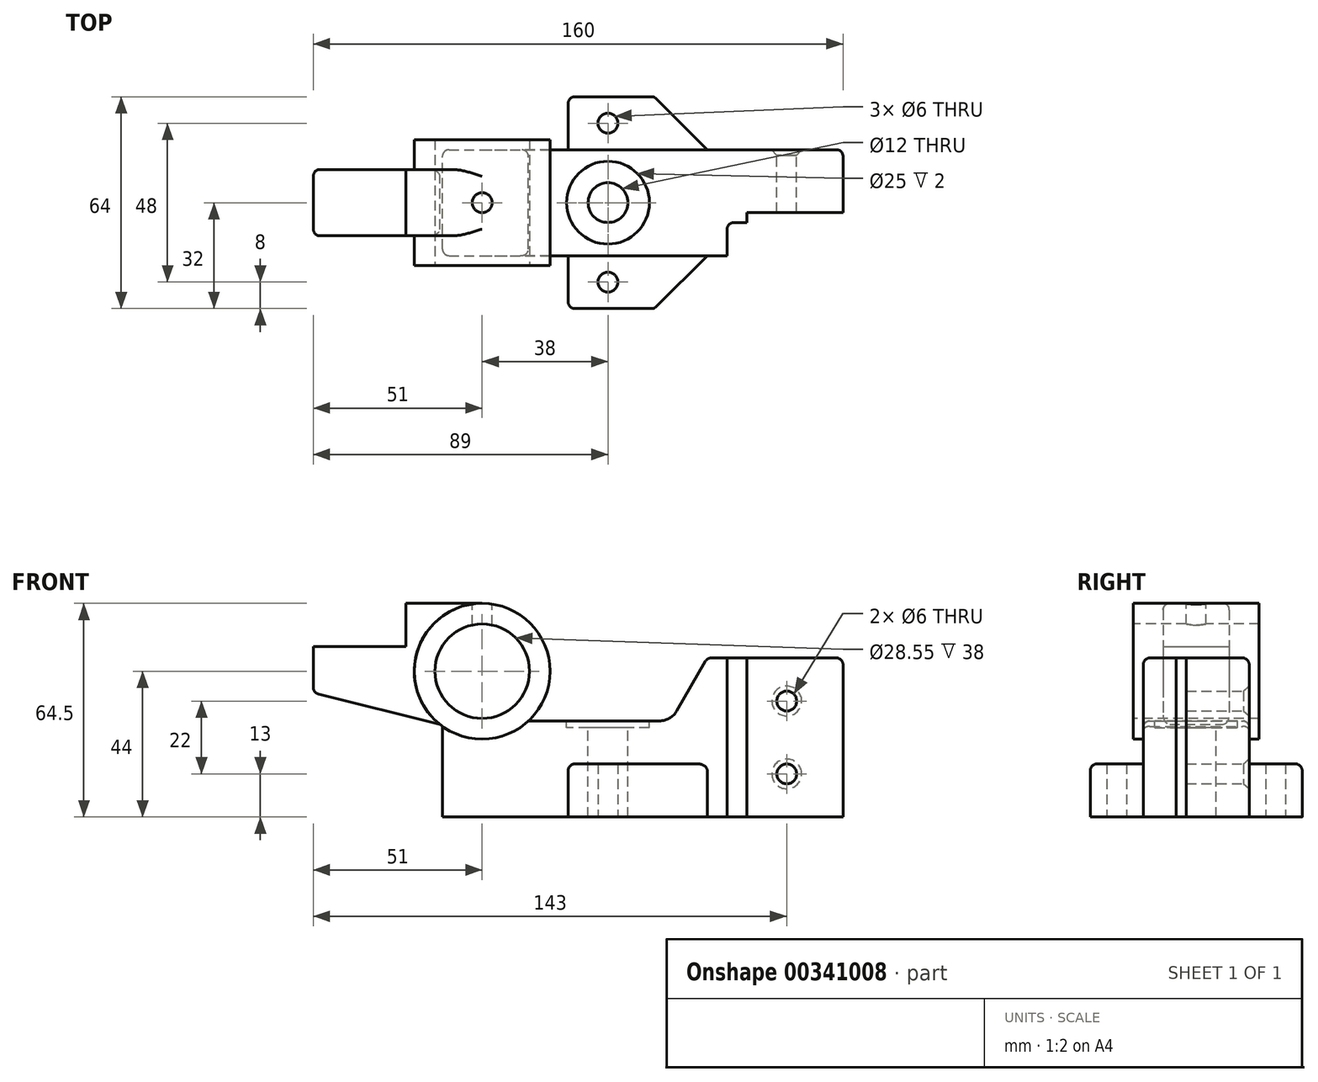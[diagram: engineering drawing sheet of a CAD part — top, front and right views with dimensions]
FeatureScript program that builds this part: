
annotation { "Feature Type Name" : "Feature", "Feature Type Description" : "" }
export const myFeature = defineFeature(function(context is Context, id is Id, definition is map)
    precondition{}
    {
        {
            var Q0;
            Q0=qCreatedBy(makeId("Front.planeOp"),FACE);
            var sketch = newSketch(context, id + "F0", { "sketchPlane" : qUnion([Q0])});
            skLineSegment(sketch, "E0", {"start": v(0, 0) * mm, "end": v(0, 48) * mm});
            skLineSegment(sketch, "E1", {"start": v(0, 48) * mm, "end": v(-41, 48) * mm});
            skLineSegment(sketch, "E2", {"start": v(-41, 48) * mm, "end": v(-50.24, 32) * mm});
            skLineSegment(sketch, "E3", {"start": v(-55.43, 29) * mm, "end": v(-95.03, 29) * mm});
            skLineSegment(sketch, "E4", {"start": v(-109, 64.5) * mm, "end": v(-132, 64.5) * mm});
            skLineSegment(sketch, "E5", {"start": v(-132, 64.5) * mm, "end": v(-132, 51.5) * mm});
            skLineSegment(sketch, "E6", {"start": v(-132, 51.5) * mm, "end": v(-160, 51.5) * mm});
            skLineSegment(sketch, "E7", {"start": v(-160, 51.5) * mm, "end": v(-160, 37.5) * mm});
            skLineSegment(sketch, "E8", {"start": v(-160, 37.5) * mm, "end": v(-121.78, 27.97) * mm});
            skLineSegment(sketch, "E9", {"start": v(-121, 27.38) * mm, "end": v(-121, 0) * mm});
            skLineSegment(sketch, "E10", {"start": v(-121, 0) * mm, "end": v(0, 0) * mm});
            skCircle(sketch, "E11", {"center": v(-109, 44) * mm, "radius": 20.5 * mm});
            skPoint(sketch, "E12.visualSharp", {"position": v(-51.97, 29) * mm});
            skArc(sketch, "E13.filletArc", {"start": v(-55.43, 29) * mm, "mid": v(-52.43, 29.8) * mm, "end": v(-50.24, 32) * mm});
            skSolve(sketch);
        }
        {
            var Q0;
            Q0=makeQuery(id+"F0.imprint","IMPRINT",FACE,{"disambiguationData":[TD([[makeQuery(id+"F0.imprint","IMPRINT",EDGE,{"derivedFrom":sQuery(id+"F0.wireOp",EDGE,"E0")}),1.0]])]});
            var Q1;
            {var subQ0=sQuery(id+"F0.wireOp",EDGE,"E11");var subQ1=makeQuery(id+"F0.imprint","INTERSECT",VERTEX,{"derivedFrom":[sQuery(id+"F0.wireOp",EDGE,"E4"),subQ0]});Q1=makeQuery(id+"F0.imprint","IMPRINT",FACE,{"disambiguationData":[TD([[makeQuery(id+"F0.imprint","IMPRINT",EDGE,{"disambiguationData":[TD([[subQ1,-1.0]])],"derivedFrom":subQ0}),1.0]])]});}
            extrude(context, id + "F1", {"entities" : qUnion([Q0, Q1]), "depth" : 32 * mm});
        }
        {
            var Q0;
            {var subQ0=sQuery(id+"F0.wireOp",EDGE,"E11");var subQ1=makeQuery(id+"F0.imprint","INTERSECT",VERTEX,{"derivedFrom":[sQuery(id+"F0.wireOp",EDGE,"E4"),subQ0]});Q0=makeQuery(id+"F0.imprint","IMPRINT",FACE,{"disambiguationData":[TD([[makeQuery(id+"F0.imprint","IMPRINT",EDGE,{"disambiguationData":[TD([[subQ1,-1.0]])],"derivedFrom":subQ0}),1.0]])]});}
            extrude(context, id + "F2", {"entities" : qUnion([Q0]), "operationType" : NewBodyOperationType.ADD, "depth" : 35 * mm, "hasSecondDirection" : true, "secondDirectionOppositeDirection" : true, "secondDirectionDepth" : 3 * mm});
        }
        {
            var Q0;
            {var subQ0=sQuery(id+"F0.wireOp",EDGE,"E4");Q0=makeQuery(id+"F0.imprint","IMPRINT",FACE,{"disambiguationData":[TD([[makeQuery(id+"F0.imprint","IMPRINT",EDGE,{"derivedFrom":subQ0}),1.0]])]});}
            extrude(context, id + "F3", {"entities" : qUnion([Q0]), "operationType" : NewBodyOperationType.ADD, "depth" : 26 * mm, "hasSecondDirection" : true, "secondDirectionOppositeDirection" : false, "secondDirectionDepth" : 6 * mm});
        }
        {
            var Q0;
            Q0=makeQuery(id+"F1.opExtrude","SWEPT_FACE",FACE,{"disambiguationData":[OSD([sQuery(id+"F0.wireOp",EDGE,"E1")])]});
            var sketch = newSketch(context, id + "F4", { "sketchPlane" : qUnion([Q0])});
            skLineSegment(sketch, "E14", {"start": v(0, -19) * mm, "end": v(-29, -19) * mm});
            skLineSegment(sketch, "E15", {"start": v(-29, -19) * mm, "end": v(-29, -22) * mm});
            skLineSegment(sketch, "E16", {"start": v(-29, -22) * mm, "end": v(-35, -22) * mm});
            skLineSegment(sketch, "E17", {"start": v(-35, -22) * mm, "end": v(-35, -32) * mm});
            skSolve(sketch);
        }
        {
            var Q0;
            {var subQ1=sQuery(id+"F4.wireOp",EDGE,"E14");Q0=makeQuery(id+"F4.imprint","IMPRINT",FACE,{"disambiguationData":[TD([[makeQuery(id+"F4.imprint","IMPRINT",EDGE,{"derivedFrom":subQ1}),1.0]])]});}
            extrude(context, id + "F5", {"entities" : qUnion([Q0]), "operationType" : NewBodyOperationType.REMOVE, "endBound" : BoundingType.THROUGH_ALL, "oppositeDirection" : true, "depth" : 25 * mm});
        }
        {
            var Q0;
            Q0=makeQuery(id+"F2.opExtrude","CAP_FACE",FACE,{"disambiguationData":[OSD([sQuery(id+"F0.wireOp",EDGE,"E11")])],"isStart":false});
            var sketch = newSketch(context, id + "F6", { "sketchPlane" : qUnion([Q0])});
            skCircle(sketch, "E18.0", {"center": v(-109, 44) * mm, "radius": 20.5 * mm});
            skSolve(sketch);
        }
        {
            var Q0;
            Q0=sQuery(id+"F6.wireOp",VERTEX,"E18.0.center");
            var Q1;
            Q1=makeQuery(id+"F1.opExtrude","SWEPT_BODY",BODY,{"disambiguationData":[OSD([sQuery(id+"F0.wireOp",EDGE,"E0"),sQuery(id+"F0.wireOp",EDGE,"E1"),sQuery(id+"F0.wireOp",EDGE,"E2"),sQuery(id+"F0.wireOp",EDGE,"E3"),sQuery(id+"F0.wireOp",EDGE,"E4"),sQuery(id+"F0.wireOp",EDGE,"E5"),sQuery(id+"F0.wireOp",EDGE,"E6"),sQuery(id+"F0.wireOp",EDGE,"E7"),sQuery(id+"F0.wireOp",EDGE,"E8"),sQuery(id+"F0.wireOp",EDGE,"E9"),sQuery(id+"F0.wireOp",EDGE,"E10"),sQuery(id+"F0.wireOp",EDGE,"E11"),sQuery(id+"F0.wireOp",EDGE,"E12.filletArc")])]});
            hole(context, id + "F7", {"style" : HoleStyle.SIMPLE, "endStyle" : HoleEndStyle.THROUGH, "holeDiameter" : 28.55 * mm, "tappedDepth" : 12 * mm, "tapClearance" : 3, "locations" : qUnion([Q0]), "scope" : qUnion([Q1])});
        }
        {
            var Q0;
            Q0=makeQuery(id+"F3.opExtrude","SWEPT_FACE",FACE,{"disambiguationData":[OSD([sQuery(id+"F0.wireOp",EDGE,"E4")])]});
            var sketch = newSketch(context, id + "F8", { "sketchPlane" : qUnion([Q0])});
            skPoint(sketch, "E19.endSnap0", {"position": v(-109, -16) * mm});
            skSolve(sketch);
        }
        {
            var Q0;
            Q0=sQuery(id+"F8.wireOp",VERTEX,"E19.endSnap0");
            var Q1;
            Q1=makeQuery(id+"F1.opExtrude","SWEPT_BODY",BODY,{"disambiguationData":[OSD([sQuery(id+"F0.wireOp",EDGE,"E0"),sQuery(id+"F0.wireOp",EDGE,"E1"),sQuery(id+"F0.wireOp",EDGE,"E2"),sQuery(id+"F0.wireOp",EDGE,"E3"),sQuery(id+"F0.wireOp",EDGE,"E4"),sQuery(id+"F0.wireOp",EDGE,"E5"),sQuery(id+"F0.wireOp",EDGE,"E6"),sQuery(id+"F0.wireOp",EDGE,"E7"),sQuery(id+"F0.wireOp",EDGE,"E8"),sQuery(id+"F0.wireOp",EDGE,"E9"),sQuery(id+"F0.wireOp",EDGE,"E10"),sQuery(id+"F0.wireOp",EDGE,"E11"),sQuery(id+"F0.wireOp",EDGE,"E12.filletArc")])]});
            hole(context, id + "F9", {"style" : HoleStyle.SIMPLE, "endStyle" : HoleEndStyle.BLIND, "holeDiameter" : 6 * mm, "holeDepth" : 12 * mm, "tappedDepth" : 12 * mm, "tapClearance" : 3, "locations" : qUnion([Q0]), "scope" : qUnion([Q1])});
        }
        {
            var Q0;
            Q0=makeQuery(id+"F1.opExtrude","SWEPT_FACE",FACE,{"disambiguationData":[OSD([sQuery(id+"F0.wireOp",EDGE,"E3")])]});
            var sketch = newSketch(context, id + "F10", { "sketchPlane" : qUnion([Q0])});
            skPoint(sketch, "E20.end.orphan", {"position": v(-71, -16) * mm});
            skPoint(sketch, "E20.start.orphan", {"position": v(-55.43, -16) * mm});
            skCircle(sketch, "E21.0", {"center": v(-109, -16) * mm, "radius": 3 * mm});
            skSolve(sketch);
        }
        {
            var Q0;
            Q0=sQuery(id+"F10.wireOp",VERTEX,"E20.end.orphan");
            var Q1;
            Q1=makeQuery(id+"F1.opExtrude","SWEPT_BODY",BODY,{"disambiguationData":[OSD([sQuery(id+"F0.wireOp",EDGE,"E0"),sQuery(id+"F0.wireOp",EDGE,"E1"),sQuery(id+"F0.wireOp",EDGE,"E2"),sQuery(id+"F0.wireOp",EDGE,"E3"),sQuery(id+"F0.wireOp",EDGE,"E4"),sQuery(id+"F0.wireOp",EDGE,"E5"),sQuery(id+"F0.wireOp",EDGE,"E6"),sQuery(id+"F0.wireOp",EDGE,"E7"),sQuery(id+"F0.wireOp",EDGE,"E8"),sQuery(id+"F0.wireOp",EDGE,"E9"),sQuery(id+"F0.wireOp",EDGE,"E10"),sQuery(id+"F0.wireOp",EDGE,"E11"),sQuery(id+"F0.wireOp",EDGE,"E12.filletArc")])]});
            hole(context, id + "F11", {"style" : HoleStyle.C_BORE, "endStyle" : HoleEndStyle.THROUGH, "holeDiameter" : 12 * mm, "cBoreDiameter" : 25 * mm, "cBoreDepth" : 2 * mm, "tappedDepth" : 12 * mm, "tapClearance" : 3, "locations" : qUnion([Q0]), "scope" : qUnion([Q1])});
        }
        {
            var Q0;
            {var subQ0=sQuery(id+"F0.wireOp",EDGE,"E2");var subQ1=sQuery(id+"F0.wireOp",EDGE,"E12.filletArc");var subQ2=sQuery(id+"F0.wireOp",EDGE,"E11");var subQ3=sQuery(id+"F0.wireOp",EDGE,"E1");var subQ4=sQuery(id+"F0.wireOp",EDGE,"E3");var subQ5=sQuery(id+"F0.wireOp",EDGE,"E4");var subQ6=sQuery(id+"F0.wireOp",EDGE,"E0");var subQ7=sQuery(id+"F0.wireOp",EDGE,"E9");var subQ8=sQuery(id+"F0.wireOp",EDGE,"E10");var subQ9=sQuery(id+"F0.wireOp",EDGE,"E8");Q0=makeQuery(id+"F2.boolean.opBoolean","SPLIT",FACE,{"disambiguationData":[TD([makeQuery(id+"F1.opExtrude","SWEPT_FACE",FACE,{"disambiguationData":[OSD([subQ6])]})])],"derivedFrom":makeQuery(id+"F1.opExtrude","CAP_FACE",FACE,{"disambiguationData":[OSD([subQ6,subQ3,subQ0,subQ4,subQ5,sQuery(id+"F0.wireOp",EDGE,"E5"),sQuery(id+"F0.wireOp",EDGE,"E6"),sQuery(id+"F0.wireOp",EDGE,"E7"),subQ9,subQ7,subQ8,subQ2,subQ1])],"isStart":true})});}
            var sketch = newSketch(context, id + "F12", { "sketchPlane" : qUnion([Q0])});
            skPoint(sketch, "E22.0", {"position": v(71, 29) * mm});
            skLineSegment(sketch, "E23", {"start": v(17, 48) * mm, "end": v(17, 0) * mm, "construction": true});
            skLineSegment(sketch, "E24", {"start": v(0, 13) * mm, "end": v(17, 13) * mm, "construction": true});
            skLineSegment(sketch, "E25", {"start": v(0, 35) * mm, "end": v(17, 35) * mm, "construction": true});
            skSolve(sketch);
        }
        {
            var Q0;
            Q0=sQuery(id+"F12.wireOp",VERTEX,"E25.end");
            var Q1;
            Q1=sQuery(id+"F12.wireOp",VERTEX,"E24.end");
            var Q2;
            Q2=makeQuery(id+"F1.opExtrude","SWEPT_BODY",BODY,{"disambiguationData":[OSD([sQuery(id+"F0.wireOp",EDGE,"E0"),sQuery(id+"F0.wireOp",EDGE,"E1"),sQuery(id+"F0.wireOp",EDGE,"E2"),sQuery(id+"F0.wireOp",EDGE,"E3"),sQuery(id+"F0.wireOp",EDGE,"E4"),sQuery(id+"F0.wireOp",EDGE,"E5"),sQuery(id+"F0.wireOp",EDGE,"E6"),sQuery(id+"F0.wireOp",EDGE,"E7"),sQuery(id+"F0.wireOp",EDGE,"E8"),sQuery(id+"F0.wireOp",EDGE,"E9"),sQuery(id+"F0.wireOp",EDGE,"E10"),sQuery(id+"F0.wireOp",EDGE,"E11"),sQuery(id+"F0.wireOp",EDGE,"E12.filletArc")])]});
            hole(context, id + "F13", {"style" : HoleStyle.C_SINK, "endStyle" : HoleEndStyle.THROUGH, "holeDiameter" : 6 * mm, "cSinkDiameter" : 9 * mm, "cSinkAngle" : 82 * degree, "tappedDepth" : 12 * mm, "tapClearance" : 3, "locations" : qUnion([Q0, Q1]), "scope" : qUnion([Q2])});
        }
        {
            var Q0;
            Q0=makeQuery(id+"F1.opExtrude","SWEPT_FACE",FACE,{"disambiguationData":[OSD([sQuery(id+"F0.wireOp",EDGE,"E10")])]});
            var sketch = newSketch(context, id + "F14", { "sketchPlane" : qUnion([Q0])});
            skLineSegment(sketch, "E26.0", {"start": v(-121, 32) * mm, "end": v(-121, 0) * mm});
            skLineSegment(sketch, "E26.1", {"start": v(-121, 0) * mm, "end": v(0, 0) * mm});
            skLineSegment(sketch, "E26.2", {"start": v(-121, 32) * mm, "end": v(-35, 32) * mm});
            skLineSegment(sketch, "E26.3", {"start": v(0, 19) * mm, "end": v(0, 0) * mm});
            skLineSegment(sketch, "E27", {"start": v(-83, 32) * mm, "end": v(-83, 48) * mm});
            skLineSegment(sketch, "E28", {"start": v(-83, 48) * mm, "end": v(-57, 48) * mm});
            skLineSegment(sketch, "E29", {"start": v(-57, 48) * mm, "end": v(-41, 32) * mm});
            skLineSegment(sketch, "E30", {"start": v(-121, 16) * mm, "end": v(0, 16) * mm, "construction": true});
            skLineSegment(sketch, "E31.MirrorCS", {"start": v(-83, 0) * mm, "end": v(-83, -16) * mm});
            skLineSegment(sketch, "E32.MirrorCS", {"start": v(-83, -16) * mm, "end": v(-57, -16) * mm});
            skLineSegment(sketch, "E33.MirrorCS", {"start": v(-57, -16) * mm, "end": v(-41, 0) * mm});
            skCircle(sketch, "E34.0", {"center": v(-71, 16) * mm, "radius": 6 * mm});
            skLineSegment(sketch, "E35", {"start": v(-71, 40) * mm, "end": v(-71, -8) * mm, "construction": true});
            skSolve(sketch);
        }
        {
            var Q0;
            {var subQ0=sQuery(id+"F14.wireOp",EDGE,"E31.MirrorCS");Q0=makeQuery(id+"F14.imprint","IMPRINT",FACE,{"disambiguationData":[TD([[makeQuery(id+"F14.imprint","IMPRINT",EDGE,{"derivedFrom":subQ0}),1.0]])]});}
            var Q1;
            {var subQ0=sQuery(id+"F14.wireOp",EDGE,"E27");Q1=makeQuery(id+"F14.imprint","IMPRINT",FACE,{"disambiguationData":[TD([[makeQuery(id+"F14.imprint","IMPRINT",EDGE,{"derivedFrom":subQ0}),-1.0]])]});}
            extrude(context, id + "F15", {"entities" : qUnion([Q0, Q1]), "operationType" : NewBodyOperationType.ADD, "oppositeDirection" : true, "depth" : 16 * mm});
        }
        {
            var Q0;
            Q0=sQuery(id+"F14.wireOp",VERTEX,"E35.start");
            var Q1;
            Q1=sQuery(id+"F14.wireOp",VERTEX,"E35.end");
            var Q2;
            Q2=makeQuery(id+"F1.opExtrude","SWEPT_BODY",BODY,{"disambiguationData":[OSD([sQuery(id+"F0.wireOp",EDGE,"E0"),sQuery(id+"F0.wireOp",EDGE,"E1"),sQuery(id+"F0.wireOp",EDGE,"E2"),sQuery(id+"F0.wireOp",EDGE,"E3"),sQuery(id+"F0.wireOp",EDGE,"E4"),sQuery(id+"F0.wireOp",EDGE,"E5"),sQuery(id+"F0.wireOp",EDGE,"E6"),sQuery(id+"F0.wireOp",EDGE,"E7"),sQuery(id+"F0.wireOp",EDGE,"E8"),sQuery(id+"F0.wireOp",EDGE,"E9"),sQuery(id+"F0.wireOp",EDGE,"E10"),sQuery(id+"F0.wireOp",EDGE,"E11"),sQuery(id+"F0.wireOp",EDGE,"E12.filletArc")])]});
            hole(context, id + "F16", {"style" : HoleStyle.SIMPLE, "endStyle" : HoleEndStyle.THROUGH, "holeDiameter" : 6 * mm, "tappedDepth" : 12 * mm, "tapClearance" : 3, "locations" : qUnion([Q0, Q1]), "scope" : qUnion([Q2])});
        }
        {
            var Q0;
            Q0=makeQuery(id+"F15.opExtrude","CAP_EDGE",EDGE,{"disambiguationData":[OSD([sQuery(id+"F14.wireOp",EDGE,"E27")])],"isStart":false});
            var Q1;
            Q1=makeQuery(id+"F15.opExtrude","CAP_EDGE",EDGE,{"disambiguationData":[OSD([sQuery(id+"F14.wireOp",EDGE,"E26.2")])],"isStart":false});
            var Q2;
            Q2=makeQuery(id+"F15.opExtrude","CAP_EDGE",EDGE,{"disambiguationData":[OSD([sQuery(id+"F14.wireOp",EDGE,"E28")])],"isStart":false});
            var Q3;
            Q3=makeQuery(id+"F15.opExtrude","CAP_EDGE",EDGE,{"disambiguationData":[OSD([sQuery(id+"F14.wireOp",EDGE,"E29")])],"isStart":false});
            var Q4;
            Q4=makeQuery(id+"F15.opExtrude","CAP_EDGE",EDGE,{"disambiguationData":[OSD([sQuery(id+"F14.wireOp",EDGE,"E33.MirrorCS")])],"isStart":false});
            var Q5;
            Q5=makeQuery(id+"F15.opExtrude","CAP_EDGE",EDGE,{"disambiguationData":[OSD([sQuery(id+"F14.wireOp",EDGE,"E32.MirrorCS")])],"isStart":false});
            var Q6;
            Q6=makeQuery(id+"F15.opExtrude","CAP_EDGE",EDGE,{"disambiguationData":[OSD([sQuery(id+"F14.wireOp",EDGE,"E31.MirrorCS")])],"isStart":false});
            var Q7;
            Q7=makeQuery(id+"F15.opExtrude","CAP_EDGE",EDGE,{"disambiguationData":[OSD([sQuery(id+"F14.wireOp",EDGE,"E26.1")])],"isStart":false});
            var Q8;
            Q8=makeQuery(id+"F15.opExtrude","SWEPT_EDGE",EDGE,{"disambiguationData":[OSD([sQuery(id+"F14.wireOp",EDGE,"E31.MirrorCS"),sQuery(id+"F14.wireOp",EDGE,"E32.MirrorCS")])]});
            var Q9;
            Q9=makeQuery(id+"F15.opExtrude","SWEPT_EDGE",EDGE,{"disambiguationData":[OSD([sQuery(id+"F14.wireOp",EDGE,"E32.MirrorCS"),sQuery(id+"F14.wireOp",EDGE,"E33.MirrorCS")])]});
            var Q10;
            Q10=makeQuery(id+"F15.opExtrude","SWEPT_EDGE",EDGE,{"disambiguationData":[OSD([sQuery(id+"F14.wireOp",EDGE,"E27"),sQuery(id+"F14.wireOp",EDGE,"E28")])]});
            var Q11;
            Q11=makeQuery(id+"F15.opExtrude","SWEPT_EDGE",EDGE,{"disambiguationData":[OSD([sQuery(id+"F14.wireOp",EDGE,"E28"),sQuery(id+"F14.wireOp",EDGE,"E29")])]});
            fillet(context, id + "F17", {"entities" : qUnion([Q0, Q1, Q2, Q3, Q4, Q5, Q6, Q7, Q8, Q9, Q10, Q11]), "radius" : 2 * mm, "tangentPropagation" : true, "allowEdgeOverflow" : false});
        }
        {
            var Q0;
            Q0=makeQuery(id+"F1.opExtrude","CAP_EDGE",EDGE,{"disambiguationData":[OSD([sQuery(id+"F0.wireOp",EDGE,"E0")])],"isStart":true});
            var Q1;
            Q1=makeQuery(id+"F1.opExtrude","SWEPT_EDGE",EDGE,{"disambiguationData":[OSD([sQuery(id+"F0.wireOp",EDGE,"E0"),sQuery(id+"F0.wireOp",EDGE,"E1")])]});
            var Q2;
            Q2=makeQuery(id+"F1.opExtrude","CAP_EDGE",EDGE,{"disambiguationData":[OSD([sQuery(id+"F0.wireOp",EDGE,"E1")])],"isStart":true});
            var Q3;
            Q3=makeQuery(id+"F1.opExtrude","SWEPT_EDGE",EDGE,{"disambiguationData":[OSD([sQuery(id+"F0.wireOp",EDGE,"E1"),sQuery(id+"F0.wireOp",EDGE,"E2")])]});
            var Q4;
            Q4=makeQuery(id+"F1.opExtrude","CAP_EDGE",EDGE,{"disambiguationData":[OSD([sQuery(id+"F0.wireOp",EDGE,"E1")])],"isStart":false});
            var Q5;
            Q5=makeQuery(id+"F5.boolean.opBoolean","COPY",EDGE,{"derivedFrom":makeQuery(id+"F5.opExtrude","CAP_EDGE",EDGE,{"disambiguationData":[OSD([sQuery(id+"F4.wireOp",EDGE,"E17")])],"isStart":true})});
            var Q6;
            Q6=makeQuery(id+"F5.boolean.opBoolean","COPY",EDGE,{"derivedFrom":makeQuery(id+"F5.opExtrude","CAP_EDGE",EDGE,{"disambiguationData":[OSD([sQuery(id+"F4.wireOp",EDGE,"E16")])],"isStart":true})});
            var Q7;
            Q7=makeQuery(id+"F5.boolean.opBoolean","COPY",EDGE,{"derivedFrom":makeQuery(id+"F5.opExtrude","SWEPT_EDGE",EDGE,{"disambiguationData":[OSD([sQuery(id+"F4.wireOp",EDGE,"E16"),sQuery(id+"F4.wireOp",EDGE,"E17")])]})});
            var Q8;
            Q8=makeQuery(id+"F5.boolean.opBoolean","COPY",EDGE,{"derivedFrom":makeQuery(id+"F5.opExtrude","SWEPT_EDGE",EDGE,{"disambiguationData":[OSD([sQuery(id+"F0.wireOp",EDGE,"E1"),sQuery(id+"F4.wireOp",EDGE,"E17")])]})});
            var Q9;
            Q9=makeQuery(id+"F1.opExtrude","CAP_EDGE",EDGE,{"disambiguationData":[OSD([sQuery(id+"F0.wireOp",EDGE,"E2")])],"isStart":false});
            var Q10;
            Q10=makeQuery(id+"F1.opExtrude","CAP_EDGE",EDGE,{"disambiguationData":[OSD([sQuery(id+"F0.wireOp",EDGE,"E2")])],"isStart":true});
            fillet(context, id + "F18", {"entities" : qUnion([Q0, Q1, Q2, Q3, Q4, Q5, Q6, Q7, Q8, Q9, Q10]), "radius" : 2 * mm, "tangentPropagation" : true, "allowEdgeOverflow" : false});
        }
        {
            var Q0;
            Q0=makeQuery(id+"F1.opExtrude","CAP_EDGE",EDGE,{"disambiguationData":[OSD([sQuery(id+"F0.wireOp",EDGE,"E3")])],"isStart":false});
            var Q1;
            Q1=makeQuery(id+"F1.opExtrude","CAP_EDGE",EDGE,{"disambiguationData":[OSD([sQuery(id+"F0.wireOp",EDGE,"E3")])],"isStart":true});
            var Q2;
            Q2=makeQuery(id+"F1.opExtrude","CAP_EDGE",EDGE,{"disambiguationData":[OSD([sQuery(id+"F0.wireOp",EDGE,"E9")])],"isStart":true});
            var Q3;
            Q3=makeQuery(id+"F1.opExtrude","CAP_EDGE",EDGE,{"disambiguationData":[OSD([sQuery(id+"F0.wireOp",EDGE,"E9")])],"isStart":false});
            fillet(context, id + "F19", {"entities" : qUnion([Q0, Q1, Q2, Q3]), "radius" : 2 * mm, "tangentPropagation" : true, "allowEdgeOverflow" : false});
        }
        {
            var Q0;
            Q0=makeQuery(id+"F3.opExtrude","CAP_EDGE",EDGE,{"disambiguationData":[OSD([sQuery(id+"F0.wireOp",EDGE,"E4")])],"isStart":false});
            var Q1;
            Q1=makeQuery(id+"F3.opExtrude","CAP_EDGE",EDGE,{"disambiguationData":[OSD([sQuery(id+"F0.wireOp",EDGE,"E4")])],"isStart":true});
            var Q2;
            Q2=makeQuery(id+"F3.opExtrude","CAP_EDGE",EDGE,{"disambiguationData":[OSD([sQuery(id+"F0.wireOp",EDGE,"E7")])],"isStart":true});
            var Q3;
            Q3=makeQuery(id+"F3.opExtrude","CAP_EDGE",EDGE,{"disambiguationData":[OSD([sQuery(id+"F0.wireOp",EDGE,"E7")])],"isStart":false});
            var Q4;
            Q4=makeQuery(id+"F3.opExtrude","SWEPT_EDGE",EDGE,{"disambiguationData":[OSD([sQuery(id+"F0.wireOp",EDGE,"E7"),sQuery(id+"F0.wireOp",EDGE,"E8")])]});
            var Q5;
            Q5=makeQuery(id+"F3.opExtrude","CAP_EDGE",EDGE,{"disambiguationData":[OSD([sQuery(id+"F0.wireOp",EDGE,"E8")])],"isStart":true});
            var Q6;
            Q6=makeQuery(id+"F3.opExtrude","CAP_EDGE",EDGE,{"disambiguationData":[OSD([sQuery(id+"F0.wireOp",EDGE,"E8")])],"isStart":false});
            var Q7;
            Q7=makeQuery(id+"F3.opExtrude","CAP_EDGE",EDGE,{"disambiguationData":[OSD([sQuery(id+"F0.wireOp",EDGE,"E11")])],"isStart":false});
            fillet(context, id + "F20", {"entities" : qUnion([Q0, Q1, Q2, Q3, Q4, Q5, Q6, Q7]), "radius" : 2 * mm, "tangentPropagation" : true, "allowEdgeOverflow" : false});
        }
    });
